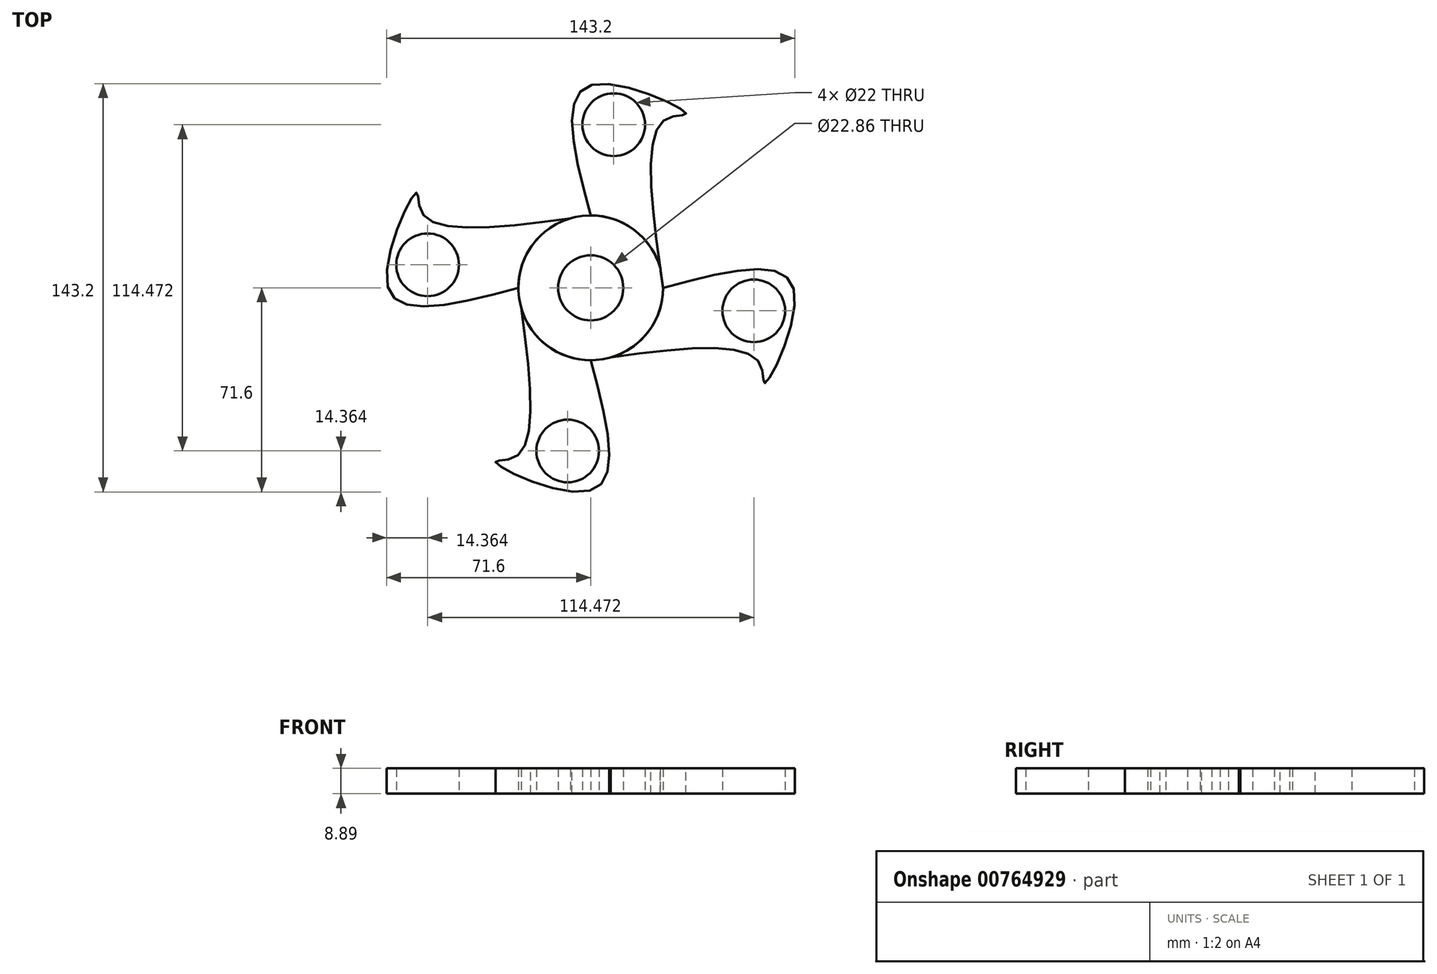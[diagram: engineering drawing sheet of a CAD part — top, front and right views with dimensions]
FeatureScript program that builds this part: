
annotation { "Feature Type Name" : "Feature", "Feature Type Description" : "" }
export const myFeature = defineFeature(function(context is Context, id is Id, definition is map)
    precondition{}
    {
        {
            var Q0;
            Q0=qCreatedBy(makeId("Top.planeOp"),FACE);
            var sketch = newSketch(context, id + "F0", { "sketchPlane" : qUnion([Q0])});
            skCircle(sketch, "E0", {"center": v(0, 0) * mm, "radius": 11.43 * mm});
            skCircle(sketch, "E1", {"center": v(0, 0) * mm, "radius": 25.4 * mm});
            skFitSpline(sketch, "E2", {"points": [v(0, 25.4) * mm, v(0, 71.1) * mm, v(33.43, 61.18) * mm, v(26.13, 59.13) * mm, v(25.4, 0) * mm], "startDerivative": vector(-58.22, 217.23) * mm, "endDerivative": vector(34.53, -242.55) * mm});
            skCircle(sketch, "E3", {"center": v(8.07, 57.24) * mm, "radius": 11 * mm});
            skSolve(sketch);
        }
        {
            var Q0;
            Q0=qCreatedBy(makeId("Front.planeOp"),FACE);
            var sketch = newSketch(context, id + "F1", { "sketchPlane" : qUnion([Q0])});
            skLineSegment(sketch, "E4", {"start": v(0, 0) * mm, "end": v(0, 43.98) * mm, "construction": true});
            skSolve(sketch);
        }
        {
            var Q0;
            Q0=makeQuery(id+"F0.imprint","IMPRINT",FACE,{"disambiguationData":[TD([[makeQuery(id+"F0.imprint","IMPRINT",EDGE,{"derivedFrom":sQuery(id+"F0.wireOp",EDGE,"E3")}),-1.0]])]});
            var Q1;
            Q1 = qSketchRegion(id + "F1", true);
            extrude(context, id + "F2", {"entities" : qUnion([Q0, Q1]), "depth" : 8.9 * mm, "offsetDistance" : 25.4 * mm});
        }
        {
            var Q0;
            Q0=qCreatedBy(makeId("Front.planeOp"),FACE);
            var sketch = newSketch(context, id + "F3", { "sketchPlane" : qUnion([Q0])});
            skLineSegment(sketch, "E5", {"start": v(0, 0) * mm, "end": v(0, 38.98) * mm, "construction": true});
            skSolve(sketch);
        }
        {
            var Q0;
            Q0=makeQuery(id+"F2.opExtrude","SWEPT_BODY",BODY,{"disambiguationData":[OSD([sQuery(id+"F0.wireOp",EDGE,"E1"),sQuery(id+"F0.wireOp",EDGE,"E2"),sQuery(id+"F0.wireOp",EDGE,"E3")])]});
            var Q1;
            Q1=sQuery(id+"F3.wireOp",EDGE,"E5");
            circularPattern(context, id + "F4", {"entities" : qUnion([Q0]), "axis" : qUnion([Q1]), "angle" : 360 * degree, "instanceCount" : 4, "equalSpace" : true});
        }
        {
            var Q0;
            Q0=makeQuery(id+"F0.imprint","IMPRINT",FACE,{"disambiguationData":[TD([[makeQuery(id+"F0.imprint","IMPRINT",EDGE,{"derivedFrom":sQuery(id+"F0.wireOp",EDGE,"E0")}),-1.0]])]});
            extrude(context, id + "F5", {"entities" : qUnion([Q0]), "depth" : 8.9 * mm, "offsetDistance" : 25.4 * mm});
        }
    });
